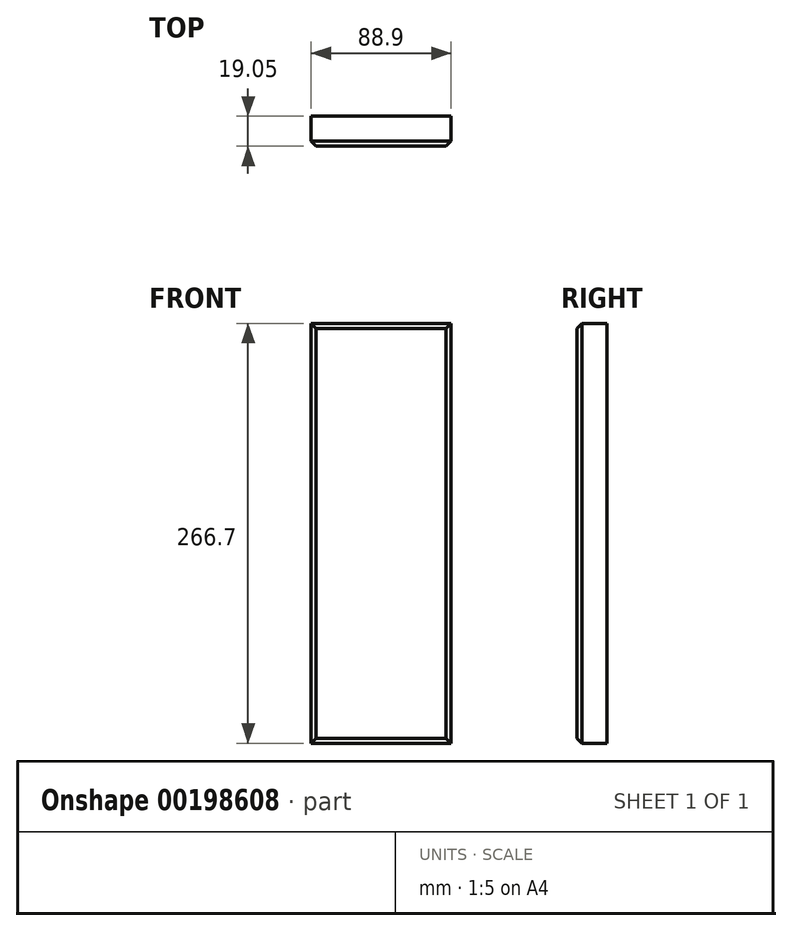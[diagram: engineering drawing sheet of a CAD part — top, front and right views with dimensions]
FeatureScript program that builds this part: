
annotation { "Feature Type Name" : "Feature", "Feature Type Description" : "" }
export const myFeature = defineFeature(function(context is Context, id is Id, definition is map)
    precondition{}
    {
        {
            var Q0;
            Q0=qCreatedBy(makeId("Top.planeOp"),FACE);
            var sketch = newSketch(context, id + "F0", { "sketchPlane" : qUnion([Q0])});
            skLineSegment(sketch, "E0.bottom", {"start": v(0, 0) * mm, "end": v(88.9, 0) * mm});
            skLineSegment(sketch, "E0.top", {"start": v(0, 19.05) * mm, "end": v(88.9, 19.05) * mm});
            skLineSegment(sketch, "E0.left", {"start": v(0, 0) * mm, "end": v(0, 19.05) * mm});
            skLineSegment(sketch, "E0.right", {"start": v(88.9, 0) * mm, "end": v(88.9, 19.05) * mm});
            skSolve(sketch);
        }
        {
            var Q0;
            Q0 = qSketchRegion(id + "F0", true);
            extrude(context, id + "F1", {"entities" : qUnion([Q0]), "depth" : 266.7 * mm});
        }
        {
            var Q0;
            Q0=makeQuery(id+"F1.opExtrude","CAP_EDGE",EDGE,{"disambiguationData":[OSD([sQuery(id+"F0.wireOp",EDGE,"E0.bottom")])],"isStart":false});
            var Q1;
            Q1=makeQuery(id+"F1.opExtrude","SWEPT_EDGE",EDGE,{"disambiguationData":[OSD([sQuery(id+"F0.wireOp",EDGE,"E0.bottom"),sQuery(id+"F0.wireOp",EDGE,"E0.left")])]});
            var Q2;
            Q2=makeQuery(id+"F1.opExtrude","SWEPT_EDGE",EDGE,{"disambiguationData":[OSD([sQuery(id+"F0.wireOp",EDGE,"E0.bottom"),sQuery(id+"F0.wireOp",EDGE,"E0.right")])]});
            var Q3;
            Q3=makeQuery(id+"F1.opExtrude","CAP_EDGE",EDGE,{"disambiguationData":[OSD([sQuery(id+"F0.wireOp",EDGE,"E0.bottom")])],"isStart":true});
            chamfer(context, id + "F2", {"entities" : qUnion([Q0, Q1, Q2, Q3]), "width" : 3.17 * mm, "tangentPropagation" : true});
        }
    });
